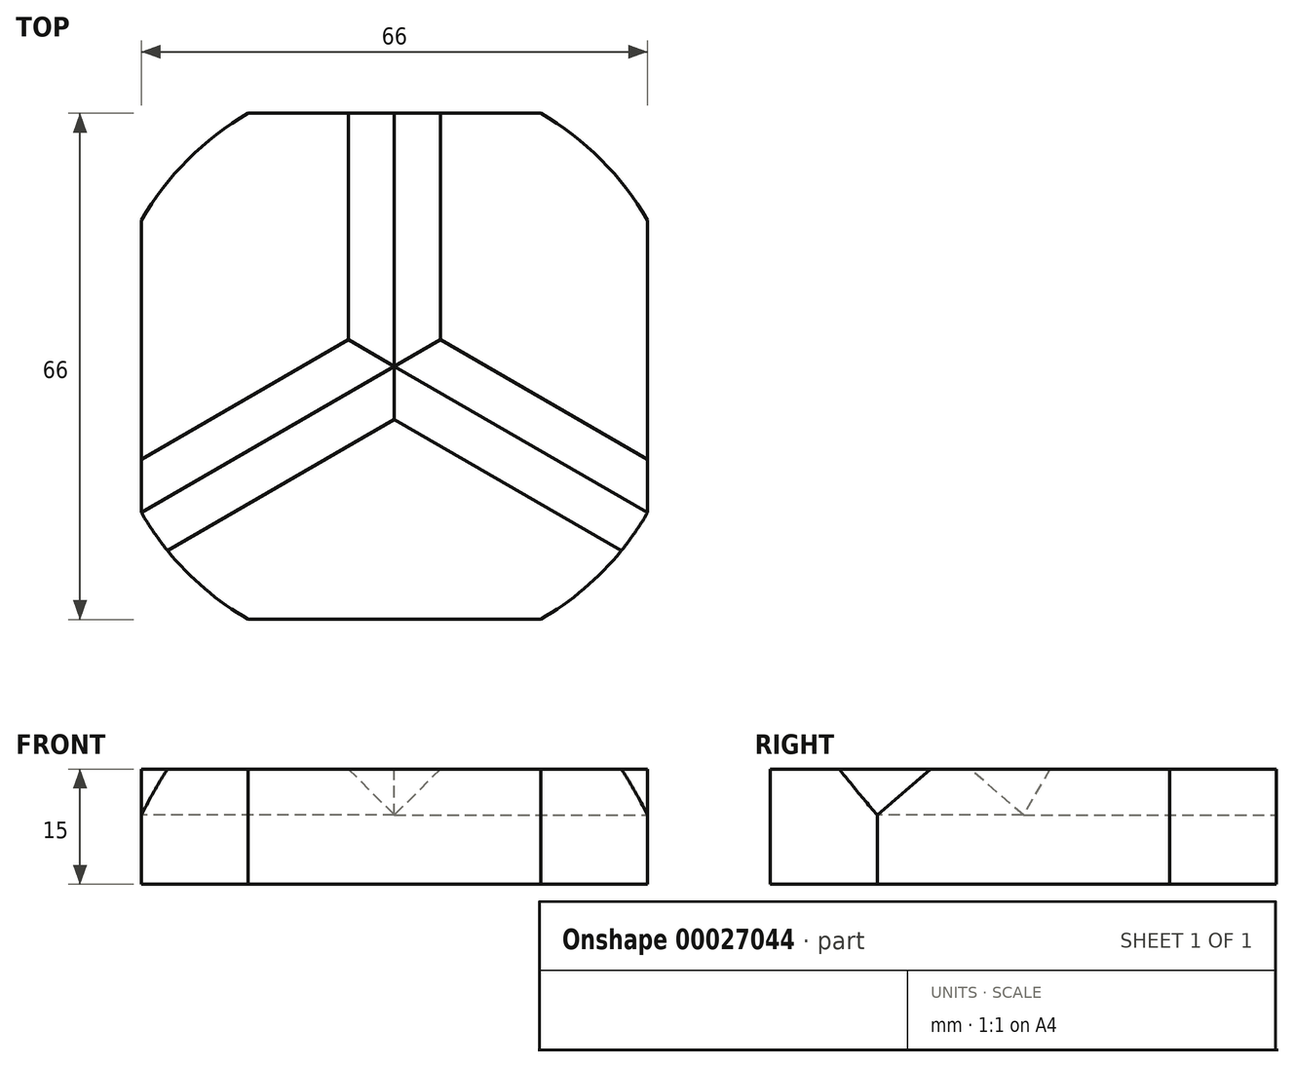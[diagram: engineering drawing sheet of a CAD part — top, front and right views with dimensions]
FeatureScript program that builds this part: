
annotation { "Feature Type Name" : "Feature", "Feature Type Description" : "" }
export const myFeature = defineFeature(function(context is Context, id is Id, definition is map)
    precondition{}
    {
        {
            var Q0;
            Q0=qCreatedBy(makeId("Top.planeOp"),FACE);
            var sketch = newSketch(context, id + "F0", { "sketchPlane" : qUnion([Q0])});
            skCircle(sketch, "E0", {"center": v(0, 0) * mm, "radius": 25.4 * mm});
            skLineSegment(sketch, "E1", {"start": v(-22, -12.7) * mm, "end": v(22, -12.7) * mm});
            skLineSegment(sketch, "E2", {"start": v(22, -12.7) * mm, "end": v(0, 25.4) * mm});
            skLineSegment(sketch, "E3", {"start": v(0, 25.4) * mm, "end": v(-22, -12.7) * mm});
            skCircle(sketch, "E4", {"center": v(0, 0) * mm, "radius": 38.1 * mm});
            skLineSegment(sketch, "E5", {"start": v(-22, -12.7) * mm, "end": v(11, 6.35) * mm});
            skLineSegment(sketch, "E6", {"start": v(22, -12.7) * mm, "end": v(-11, 6.35) * mm});
            skLineSegment(sketch, "E7", {"start": v(0, 25.4) * mm, "end": v(0, -12.7) * mm});
            skCircle(sketch, "E8", {"center": v(0, 0) * mm, "radius": 8.08 * mm});
            skLineSegment(sketch, "E9", {"start": v(22, -12.7) * mm, "end": v(33, -19.05) * mm});
            skLineSegment(sketch, "E10", {"start": v(11, 6.35) * mm, "end": v(33, 19.05) * mm});
            skLineSegment(sketch, "E11", {"start": v(0, 25.4) * mm, "end": v(0, 38.1) * mm});
            skLineSegment(sketch, "E12", {"start": v(-22, -12.7) * mm, "end": v(-33, -19.05) * mm});
            skLineSegment(sketch, "E13.rect.bottom", {"start": v(33, 33) * mm, "end": v(-33, 33) * mm});
            skLineSegment(sketch, "E13.rect.top", {"start": v(33, -33) * mm, "end": v(-33, -33) * mm});
            skLineSegment(sketch, "E13.rect.left", {"start": v(33, 33) * mm, "end": v(33, -33) * mm});
            skLineSegment(sketch, "E13.rect.right", {"start": v(-33, 33) * mm, "end": v(-33, -33) * mm});
            skSolve(sketch);
        }
        {
            var Q0;
            {var subQ5=sQuery(id+"F0.wireOp",EDGE,"E9");Q0=makeQuery(id+"F0.imprint","IMPRINT",FACE,{"disambiguationData":[TD([[makeQuery(id+"F0.imprint","IMPRINT",EDGE,{"derivedFrom":subQ5}),-1.0]])]});}
            var Q1;
            {var subQ5=sQuery(id+"F0.wireOp",EDGE,"E9");Q1=makeQuery(id+"F0.imprint","IMPRINT",FACE,{"disambiguationData":[TD([[makeQuery(id+"F0.imprint","IMPRINT",EDGE,{"derivedFrom":subQ5}),1.0]])]});}
            var Q2;
            {var subQ0=sQuery(id+"F0.wireOp",EDGE,"E10");var subQ1=sQuery(id+"F0.wireOp",EDGE,"E0");var subQ2=makeQuery(id+"F0.imprint","INTERSECT",VERTEX,{"derivedFrom":[subQ1,subQ0]});Q2=makeQuery(id+"F0.imprint","IMPRINT",FACE,{"disambiguationData":[TD([[makeQuery(id+"F0.imprint","IMPRINT",EDGE,{"disambiguationData":[TD([[subQ2,1.0]])],"derivedFrom":subQ0}),-1.0]])]});}
            var Q3;
            {var subQ0=sQuery(id+"F0.wireOp",EDGE,"E10");var subQ1=sQuery(id+"F0.wireOp",EDGE,"E0");var subQ2=makeQuery(id+"F0.imprint","INTERSECT",VERTEX,{"derivedFrom":[subQ1,subQ0]});Q3=makeQuery(id+"F0.imprint","IMPRINT",FACE,{"disambiguationData":[TD([[makeQuery(id+"F0.imprint","IMPRINT",EDGE,{"disambiguationData":[TD([[subQ2,1.0]])],"derivedFrom":subQ0}),1.0]])]});}
            var Q4;
            {var subQ0=sQuery(id+"F0.wireOp",EDGE,"E8");var subQ3=sQuery(id+"F0.wireOp",EDGE,"E5");var subQ4=makeQuery(id+"F0.imprint","INTERSECT",VERTEX,{"disambiguationData":[OD(1.0)],"derivedFrom":[subQ3,subQ0]});Q4=makeQuery(id+"F0.imprint","IMPRINT",FACE,{"disambiguationData":[TD([[makeQuery(id+"F0.imprint","IMPRINT",EDGE,{"disambiguationData":[TD([[subQ4,-1.0]])],"derivedFrom":subQ0}),-1.0]])]});}
            var Q5;
            {var subQ3=sQuery(id+"F0.wireOp",EDGE,"E6");var subQ5=sQuery(id+"F0.wireOp",EDGE,"E3");var subQ7=makeQuery(id+"F0.imprint","INTERSECT",VERTEX,{"derivedFrom":[subQ5,subQ3]});Q5=makeQuery(id+"F0.imprint","IMPRINT",FACE,{"disambiguationData":[TD([[makeQuery(id+"F0.imprint","IMPRINT",EDGE,{"disambiguationData":[TD([[subQ7,1.0]])],"derivedFrom":subQ3}),-1.0]])]});}
            var Q6;
            {var subQ0=sQuery(id+"F0.wireOp",EDGE,"E3");var subQ1=makeQuery(id+"F0.imprint","INTERSECT",VERTEX,{"derivedFrom":[subQ0,sQuery(id+"F0.wireOp",EDGE,"E6")]});Q6=makeQuery(id+"F0.imprint","IMPRINT",FACE,{"disambiguationData":[TD([[makeQuery(id+"F0.imprint","IMPRINT",EDGE,{"disambiguationData":[TD([[subQ1,1.0]])],"derivedFrom":subQ0}),-1.0]])]});}
            var Q7;
            {var subQ0=sQuery(id+"F0.wireOp",EDGE,"E8");var subQ3=sQuery(id+"F0.wireOp",EDGE,"E6");var subQ4=makeQuery(id+"F0.imprint","INTERSECT",VERTEX,{"disambiguationData":[OD(1.0)],"derivedFrom":[subQ3,subQ0]});Q7=makeQuery(id+"F0.imprint","IMPRINT",FACE,{"disambiguationData":[TD([[makeQuery(id+"F0.imprint","IMPRINT",EDGE,{"disambiguationData":[TD([[subQ4,1.0]])],"derivedFrom":subQ0}),1.0]])]});}
            var Q8;
            {var subQ1=sQuery(id+"F0.wireOp",EDGE,"E6");var subQ5=sQuery(id+"F0.wireOp",EDGE,"E3");var subQ6=makeQuery(id+"F0.imprint","INTERSECT",VERTEX,{"derivedFrom":[subQ5,subQ1]});Q8=makeQuery(id+"F0.imprint","IMPRINT",FACE,{"disambiguationData":[TD([[makeQuery(id+"F0.imprint","IMPRINT",EDGE,{"disambiguationData":[TD([[subQ6,1.0]])],"derivedFrom":subQ1}),1.0]])]});}
            var Q9;
            {var subQ0=sQuery(id+"F0.wireOp",EDGE,"E8");var subQ3=sQuery(id+"F0.wireOp",EDGE,"E5");var subQ4=makeQuery(id+"F0.imprint","INTERSECT",VERTEX,{"disambiguationData":[OD(0.0)],"derivedFrom":[subQ3,subQ0]});Q9=makeQuery(id+"F0.imprint","IMPRINT",FACE,{"disambiguationData":[TD([[makeQuery(id+"F0.imprint","IMPRINT",EDGE,{"disambiguationData":[TD([[subQ4,1.0]])],"derivedFrom":subQ0}),1.0]])]});}
            var Q10;
            {var subQ0=sQuery(id+"F0.wireOp",EDGE,"E8");var subQ3=sQuery(id+"F0.wireOp",EDGE,"E5");var subQ4=makeQuery(id+"F0.imprint","INTERSECT",VERTEX,{"disambiguationData":[OD(0.0)],"derivedFrom":[subQ3,subQ0]});Q10=makeQuery(id+"F0.imprint","IMPRINT",FACE,{"disambiguationData":[TD([[makeQuery(id+"F0.imprint","IMPRINT",EDGE,{"disambiguationData":[TD([[subQ4,-1.0]])],"derivedFrom":subQ0}),1.0]])]});}
            var Q11;
            {var subQ0=sQuery(id+"F0.wireOp",EDGE,"E8");var subQ3=sQuery(id+"F0.wireOp",EDGE,"E6");var subQ4=makeQuery(id+"F0.imprint","INTERSECT",VERTEX,{"disambiguationData":[OD(0.0)],"derivedFrom":[subQ3,subQ0]});Q11=makeQuery(id+"F0.imprint","IMPRINT",FACE,{"disambiguationData":[TD([[makeQuery(id+"F0.imprint","IMPRINT",EDGE,{"disambiguationData":[TD([[subQ4,1.0]])],"derivedFrom":subQ0}),1.0]])]});}
            var Q12;
            {var subQ0=sQuery(id+"F0.wireOp",EDGE,"E8");var subQ3=sQuery(id+"F0.wireOp",EDGE,"E5");var subQ4=makeQuery(id+"F0.imprint","INTERSECT",VERTEX,{"disambiguationData":[OD(1.0)],"derivedFrom":[subQ3,subQ0]});Q12=makeQuery(id+"F0.imprint","IMPRINT",FACE,{"disambiguationData":[TD([[makeQuery(id+"F0.imprint","IMPRINT",EDGE,{"disambiguationData":[TD([[subQ4,1.0]])],"derivedFrom":subQ0}),1.0]])]});}
            var Q13;
            {var subQ0=sQuery(id+"F0.wireOp",EDGE,"E8");var subQ3=sQuery(id+"F0.wireOp",EDGE,"E5");var subQ4=makeQuery(id+"F0.imprint","INTERSECT",VERTEX,{"disambiguationData":[OD(1.0)],"derivedFrom":[subQ3,subQ0]});Q13=makeQuery(id+"F0.imprint","IMPRINT",FACE,{"disambiguationData":[TD([[makeQuery(id+"F0.imprint","IMPRINT",EDGE,{"disambiguationData":[TD([[subQ4,-1.0]])],"derivedFrom":subQ0}),1.0]])]});}
            var Q14;
            {var subQ1=sQuery(id+"F0.wireOp",EDGE,"E7");var subQ5=sQuery(id+"F0.wireOp",EDGE,"E1");var subQ6=makeQuery(id+"F0.imprint","INTERSECT",VERTEX,{"derivedFrom":[subQ5,subQ1]});Q14=makeQuery(id+"F0.imprint","IMPRINT",FACE,{"disambiguationData":[TD([[makeQuery(id+"F0.imprint","IMPRINT",EDGE,{"disambiguationData":[TD([[subQ6,1.0]])],"derivedFrom":subQ1}),1.0]])]});}
            var Q15;
            {var subQ0=sQuery(id+"F0.wireOp",EDGE,"E8");var subQ3=sQuery(id+"F0.wireOp",EDGE,"E5");var subQ4=makeQuery(id+"F0.imprint","INTERSECT",VERTEX,{"disambiguationData":[OD(1.0)],"derivedFrom":[subQ3,subQ0]});Q15=makeQuery(id+"F0.imprint","IMPRINT",FACE,{"disambiguationData":[TD([[makeQuery(id+"F0.imprint","IMPRINT",EDGE,{"disambiguationData":[TD([[subQ4,1.0]])],"derivedFrom":subQ0}),-1.0]])]});}
            var Q16;
            {var subQ0=sQuery(id+"F0.wireOp",EDGE,"E1");var subQ1=makeQuery(id+"F0.imprint","INTERSECT",VERTEX,{"derivedFrom":[subQ0,sQuery(id+"F0.wireOp",EDGE,"E7")]});Q16=makeQuery(id+"F0.imprint","IMPRINT",FACE,{"disambiguationData":[TD([[makeQuery(id+"F0.imprint","IMPRINT",EDGE,{"disambiguationData":[TD([[subQ1,1.0]])],"derivedFrom":subQ0}),-1.0]])]});}
            var Q17;
            {var subQ1=sQuery(id+"F0.wireOp",EDGE,"E7");var subQ5=sQuery(id+"F0.wireOp",EDGE,"E1");var subQ6=makeQuery(id+"F0.imprint","INTERSECT",VERTEX,{"derivedFrom":[subQ5,subQ1]});Q17=makeQuery(id+"F0.imprint","IMPRINT",FACE,{"disambiguationData":[TD([[makeQuery(id+"F0.imprint","IMPRINT",EDGE,{"disambiguationData":[TD([[subQ6,1.0]])],"derivedFrom":subQ1}),-1.0]])]});}
            var Q18;
            {var subQ0=sQuery(id+"F0.wireOp",EDGE,"2a692118-128e-4bd1-a7af-66a94f11777a.bottom");var subQ3=sQuery(id+"F0.wireOp",EDGE,"E0");var subQ4=makeQuery(id+"F0.imprint","INTERSECT",VERTEX,{"disambiguationData":[OD(1.0)],"derivedFrom":[subQ3,subQ0]});Q18=makeQuery(id+"F0.imprint","IMPRINT",FACE,{"disambiguationData":[TD([[makeQuery(id+"F0.imprint","IMPRINT",EDGE,{"disambiguationData":[TD([[subQ4,-1.0]])],"derivedFrom":subQ0}),1.0]])]});}
            var Q19;
            {var subQ0=sQuery(id+"F0.wireOp",EDGE,"2a692118-128e-4bd1-a7af-66a94f11777a.bottom");var subQ3=sQuery(id+"F0.wireOp",EDGE,"E3");var subQ4=makeQuery(id+"F0.imprint","INTERSECT",VERTEX,{"derivedFrom":[subQ3,subQ0]});Q19=makeQuery(id+"F0.imprint","IMPRINT",FACE,{"disambiguationData":[TD([[makeQuery(id+"F0.imprint","IMPRINT",EDGE,{"disambiguationData":[TD([[subQ4,-1.0]])],"derivedFrom":subQ0}),1.0]])]});}
            var Q20;
            {var subQ0=sQuery(id+"F0.wireOp",EDGE,"2a692118-128e-4bd1-a7af-66a94f11777a.bottom");var subQ3=sQuery(id+"F0.wireOp",EDGE,"E2");var subQ4=makeQuery(id+"F0.imprint","INTERSECT",VERTEX,{"derivedFrom":[subQ3,subQ0]});Q20=makeQuery(id+"F0.imprint","IMPRINT",FACE,{"disambiguationData":[TD([[makeQuery(id+"F0.imprint","IMPRINT",EDGE,{"disambiguationData":[TD([[subQ4,1.0]])],"derivedFrom":subQ0}),1.0]])]});}
            var Q21;
            {var subQ0=sQuery(id+"F0.wireOp",EDGE,"2a692118-128e-4bd1-a7af-66a94f11777a.bottom");var subQ3=sQuery(id+"F0.wireOp",EDGE,"E0");var subQ4=makeQuery(id+"F0.imprint","INTERSECT",VERTEX,{"disambiguationData":[OD(0.0)],"derivedFrom":[subQ3,subQ0]});Q21=makeQuery(id+"F0.imprint","IMPRINT",FACE,{"disambiguationData":[TD([[makeQuery(id+"F0.imprint","IMPRINT",EDGE,{"disambiguationData":[TD([[subQ4,1.0]])],"derivedFrom":subQ0}),1.0]])]});}
            var Q22;
            {var subQ4=sQuery(id+"F0.wireOp",EDGE,"E12");Q22=makeQuery(id+"F0.imprint","IMPRINT",FACE,{"disambiguationData":[TD([[makeQuery(id+"F0.imprint","IMPRINT",EDGE,{"derivedFrom":subQ4}),-1.0]])]});}
            var Q23;
            {var subQ0=sQuery(id+"F0.wireOp",EDGE,"2a692118-128e-4bd1-a7af-66a94f11777a.bottom");var subQ1=sQuery(id+"F0.wireOp",EDGE,"E0");var subQ2=makeQuery(id+"F0.imprint","INTERSECT",VERTEX,{"disambiguationData":[OD(0.0)],"derivedFrom":[subQ1,subQ0]});Q23=makeQuery(id+"F0.imprint","IMPRINT",FACE,{"disambiguationData":[TD([[makeQuery(id+"F0.imprint","IMPRINT",EDGE,{"disambiguationData":[TD([[subQ2,1.0]])],"derivedFrom":subQ1}),-1.0]])]});}
            var Q24;
            {var subQ0=sQuery(id+"F0.wireOp",EDGE,"2a692118-128e-4bd1-a7af-66a94f11777a.top");var subQ1=sQuery(id+"F0.wireOp",EDGE,"E0");var subQ2=makeQuery(id+"F0.imprint","INTERSECT",VERTEX,{"disambiguationData":[OD(0.0)],"derivedFrom":[subQ1,subQ0]});Q24=makeQuery(id+"F0.imprint","IMPRINT",FACE,{"disambiguationData":[TD([[makeQuery(id+"F0.imprint","IMPRINT",EDGE,{"disambiguationData":[TD([[subQ2,-1.0]])],"derivedFrom":subQ1}),-1.0]])]});}
            var Q25;
            {var subQ0=sQuery(id+"F0.wireOp",EDGE,"2a692118-128e-4bd1-a7af-66a94f11777a.top");var subQ1=sQuery(id+"F0.wireOp",EDGE,"E0");var subQ3=makeQuery(id+"F0.imprint","INTERSECT",VERTEX,{"disambiguationData":[OD(0.0)],"derivedFrom":[subQ1,subQ0]});Q25=makeQuery(id+"F0.imprint","IMPRINT",FACE,{"disambiguationData":[TD([[makeQuery(id+"F0.imprint","IMPRINT",EDGE,{"disambiguationData":[TD([[subQ3,-1.0]])],"derivedFrom":subQ1}),1.0]])]});}
            var Q26;
            {var subQ3=sQuery(id+"F0.wireOp",EDGE,"E12");Q26=makeQuery(id+"F0.imprint","IMPRINT",FACE,{"disambiguationData":[TD([[makeQuery(id+"F0.imprint","IMPRINT",EDGE,{"derivedFrom":subQ3}),1.0]])]});}
            extrude(context, id + "F1", {"entities" : qUnion([Q0, Q1, Q2, Q3, Q4, Q5, Q6, Q7, Q8, Q9, Q10, Q11, Q12, Q13, Q14, Q15, Q16, Q17, Q18, Q19, Q20, Q21, Q22, Q23, Q24, Q25, Q26]), "depth" : 15 * mm});
        }
        {
            var Q0;
            Q0=sQuery(id+"F0.wireOp",VERTEX,"E9.end");
            var Q1;
            Q1=sQuery(id+"F0.wireOp",EDGE,"E9");
            cPlane(context, id + "F2", {"entities" : qUnion([Q0, Q1]), "cplaneType" : CPlaneType.LINE_POINT, "offset" : 150 * mm, "width" : 150 * mm, "height" : 150 * mm});
        }
        {
            var Q0;
            Q0=qCreatedBy(id+"F2.planeOp",FACE);
            var sketch = newSketch(context, id + "F3", { "sketchPlane" : qUnion([Q0])});
            skLineSegment(sketch, "E14.rect.bottom", {"start": v(-6, -6) * mm, "end": v(6, -6) * mm});
            skLineSegment(sketch, "E14.rect.left", {"start": v(-6, -6) * mm, "end": v(-6, 0) * mm});
            skPoint(sketch, "E14.rect.middle", {"position": v(0, 0) * mm});
            skLineSegment(sketch, "E15", {"start": v(6, 0) * mm, "end": v(0, 6) * mm});
            skLineSegment(sketch, "E16", {"start": v(0, 6) * mm, "end": v(-6, 0) * mm});
            skPoint(sketch, "E17.orphan", {"position": v(-6, 6) * mm});
            skPoint(sketch, "E18.orphan", {"position": v(6, 6) * mm});
            skLineSegment(sketch, "E19", {"start": v(6, -6) * mm, "end": v(6, 0) * mm});
            skLineSegment(sketch, "E20.0", {"start": v(33, 0) * mm, "end": v(38.1, 0) * mm});
            skLineSegment(sketch, "E20.1", {"start": v(33, 15) * mm, "end": v(38.1, 15) * mm});
            skLineSegment(sketch, "E21", {"start": v(38.1, 0) * mm, "end": v(38.1, 15) * mm});
            skLineSegment(sketch, "E22", {"start": v(33, 0) * mm, "end": v(33, 15) * mm});
            skLineSegment(sketch, "E23", {"start": v(33, 7.5) * mm, "end": v(38.1, 7.5) * mm});
            skLineSegment(sketch, "E24.MirrorCS", {"start": v(6, 15) * mm, "end": v(0, 9) * mm});
            skLineSegment(sketch, "E25.MirrorCS", {"start": v(6, 21) * mm, "end": v(6, 15) * mm});
            skLineSegment(sketch, "E26.MirrorCS", {"start": v(-6, 21) * mm, "end": v(6, 21) * mm});
            skLineSegment(sketch, "E27.MirrorCS", {"start": v(-6, 21) * mm, "end": v(-6, 15) * mm});
            skLineSegment(sketch, "E28.MirrorCS", {"start": v(0, 9) * mm, "end": v(-6, 15) * mm});
            skSolve(sketch);
        }
        {
            var Q0;
            {var subQ1=sQuery(id+"F3.wireOp",EDGE,"E24.MirrorCS");Q0=makeQuery(id+"F3.imprint","IMPRINT",FACE,{"disambiguationData":[TD([[makeQuery(id+"F3.imprint","IMPRINT",EDGE,{"derivedFrom":subQ1}),-1.0]])]});}
            var Q1;
            {var subQ1=sQuery(id+"F3.wireOp",EDGE,"E25.MirrorCS");Q1=makeQuery(id+"F3.imprint","IMPRINT",FACE,{"disambiguationData":[TD([[makeQuery(id+"F3.imprint","IMPRINT",EDGE,{"derivedFrom":subQ1}),-1.0]])]});}
            extrude(context, id + "F4", {"entities" : qUnion([Q0, Q1]), "operationType" : NewBodyOperationType.REMOVE, "oppositeDirection" : true, "depth" : 38.1 * mm});
        }
        {
            var Q0;
            Q0=sQuery(id+"F0.wireOp",VERTEX,"E11.end");
            var Q1;
            Q1=sQuery(id+"F0.wireOp",EDGE,"E11");
            cPlane(context, id + "F5", {"entities" : qUnion([Q0, Q1]), "cplaneType" : CPlaneType.LINE_POINT, "offset" : 150 * mm, "width" : 150 * mm, "height" : 150 * mm});
        }
        {
            var Q0;
            Q0=sQuery(id+"F0.wireOp",VERTEX,"E12.end");
            var Q1;
            Q1=sQuery(id+"F0.wireOp",EDGE,"E12");
            cPlane(context, id + "F6", {"entities" : qUnion([Q0, Q1]), "cplaneType" : CPlaneType.LINE_POINT, "offset" : 150 * mm, "width" : 150 * mm, "height" : 150 * mm});
        }
        {
            var Q0;
            Q0=qCreatedBy(id+"F5.planeOp",FACE);
            var sketch = newSketch(context, id + "F7", { "sketchPlane" : qUnion([Q0])});
            skLineSegment(sketch, "E29.rect.top", {"start": v(-6, -6) * mm, "end": v(6, -6) * mm});
            skLineSegment(sketch, "E29.rect.left", {"start": v(-6, 0) * mm, "end": v(-6, -6) * mm});
            skLineSegment(sketch, "E29.rect.right", {"start": v(6, 0) * mm, "end": v(6, -6) * mm});
            skPoint(sketch, "E29.rect.middle", {"position": v(0, 0) * mm});
            skLineSegment(sketch, "E30", {"start": v(6, 0) * mm, "end": v(0, 6) * mm});
            skLineSegment(sketch, "E31", {"start": v(0, 6) * mm, "end": v(-6, 0) * mm});
            skPoint(sketch, "E32.orphan", {"position": v(6, 6) * mm});
            skPoint(sketch, "E33.orphan", {"position": v(-6, 6) * mm});
            skLineSegment(sketch, "E34.0", {"start": v(-33, 0) * mm, "end": v(-19.05, 0) * mm});
            skLineSegment(sketch, "E34.1", {"start": v(-33, 15) * mm, "end": v(-19.05, 15) * mm});
            skLineSegment(sketch, "E35", {"start": v(-19.05, 0) * mm, "end": v(-19.05, 15) * mm});
            skLineSegment(sketch, "E36", {"start": v(-33, 0) * mm, "end": v(-33, 15) * mm});
            skLineSegment(sketch, "E37", {"start": v(-33, 7.5) * mm, "end": v(-19.05, 7.5) * mm});
            skLineSegment(sketch, "E38.MirrorCS", {"start": v(0, 9) * mm, "end": v(-6, 15) * mm});
            skLineSegment(sketch, "E39.MirrorCS", {"start": v(6, 15) * mm, "end": v(0, 9) * mm});
            skLineSegment(sketch, "E40.MirrorCS", {"start": v(6, 15) * mm, "end": v(6, 21) * mm});
            skLineSegment(sketch, "E41.MirrorCS", {"start": v(-6, 21) * mm, "end": v(6, 21) * mm});
            skLineSegment(sketch, "E42.MirrorCS", {"start": v(-6, 15) * mm, "end": v(-6, 21) * mm});
            skSolve(sketch);
        }
        {
            var Q0;
            {var subQ1=sQuery(id+"F7.wireOp",EDGE,"E38.MirrorCS");Q0=makeQuery(id+"F7.imprint","IMPRINT",FACE,{"disambiguationData":[TD([[makeQuery(id+"F7.imprint","IMPRINT",EDGE,{"derivedFrom":subQ1}),-1.0]])]});}
            var Q1;
            {var subQ1=sQuery(id+"F7.wireOp",EDGE,"E40.MirrorCS");Q1=makeQuery(id+"F7.imprint","IMPRINT",FACE,{"disambiguationData":[TD([[makeQuery(id+"F7.imprint","IMPRINT",EDGE,{"derivedFrom":subQ1}),1.0]])]});}
            extrude(context, id + "F8", {"entities" : qUnion([Q0, Q1]), "operationType" : NewBodyOperationType.REMOVE, "oppositeDirection" : true, "depth" : 38.1 * mm});
        }
        {
            var Q0;
            Q0=qCreatedBy(id+"F6.planeOp",FACE);
            var sketch = newSketch(context, id + "F9", { "sketchPlane" : qUnion([Q0])});
            skLineSegment(sketch, "E43.rect.bottom", {"start": v(-6, 6) * mm, "end": v(6, 6) * mm});
            skLineSegment(sketch, "E43.rect.top", {"start": v(-6, -6) * mm, "end": v(6, -6) * mm});
            skLineSegment(sketch, "E43.rect.left", {"start": v(-6, 6) * mm, "end": v(-6, -6) * mm});
            skLineSegment(sketch, "E43.rect.right", {"start": v(6, 6) * mm, "end": v(6, -6) * mm});
            skPoint(sketch, "E43.rect.middle", {"position": v(0, 0) * mm});
            skLineSegment(sketch, "E44", {"start": v(6, 0) * mm, "end": v(0, 6) * mm});
            skLineSegment(sketch, "E45", {"start": v(0, 6) * mm, "end": v(-6, 0) * mm});
            skLineSegment(sketch, "E46.0", {"start": v(33, 0) * mm, "end": v(38.1, 0) * mm});
            skLineSegment(sketch, "E46.1", {"start": v(0, 15) * mm, "end": v(38.1, 15) * mm});
            skLineSegment(sketch, "E47", {"start": v(33, 0) * mm, "end": v(0, 15) * mm});
            skLineSegment(sketch, "E48", {"start": v(38.1, 15) * mm, "end": v(38.1, 0) * mm});
            skLineSegment(sketch, "E49", {"start": v(16.5, 7.5) * mm, "end": v(38.1, 7.5) * mm});
            skLineSegment(sketch, "E50.MirrorCS", {"start": v(-6, 21) * mm, "end": v(6, 21) * mm});
            skLineSegment(sketch, "E51.MirrorCS", {"start": v(-6, 9) * mm, "end": v(-6, 21) * mm});
            skLineSegment(sketch, "E52.MirrorCS", {"start": v(6, 9) * mm, "end": v(6, 21) * mm});
            skLineSegment(sketch, "E53.MirrorCS", {"start": v(6, 15) * mm, "end": v(0, 9) * mm});
            skLineSegment(sketch, "E54.MirrorCS", {"start": v(0, 9) * mm, "end": v(-6, 15) * mm});
            skSolve(sketch);
        }
        {
            var Q0;
            {var subQ3=sQuery(id+"F9.wireOp",EDGE,"E50.MirrorCS");Q0=makeQuery(id+"F9.imprint","IMPRINT",FACE,{"disambiguationData":[TD([[makeQuery(id+"F9.imprint","IMPRINT",EDGE,{"derivedFrom":subQ3}),-1.0]])]});}
            var Q1;
            {var subQ1=sQuery(id+"F9.wireOp",EDGE,"E53.MirrorCS");Q1=makeQuery(id+"F9.imprint","IMPRINT",FACE,{"disambiguationData":[TD([[makeQuery(id+"F9.imprint","IMPRINT",EDGE,{"derivedFrom":subQ1}),-1.0]])]});}
            extrude(context, id + "F10", {"entities" : qUnion([Q0, Q1]), "operationType" : NewBodyOperationType.REMOVE, "oppositeDirection" : true, "depth" : 38.1 * mm});
        }
    });
